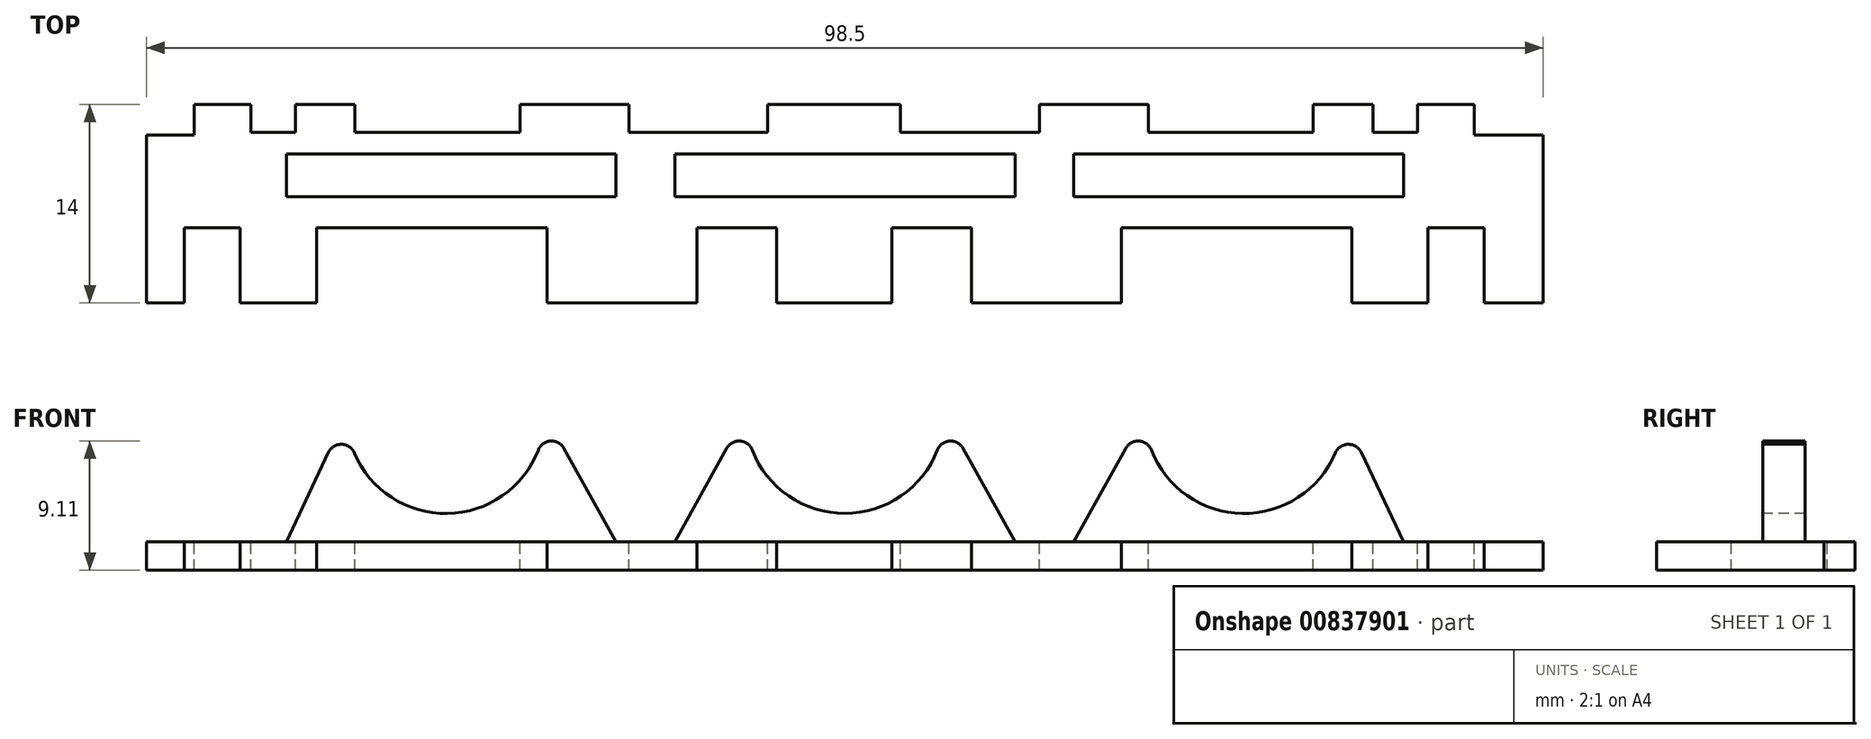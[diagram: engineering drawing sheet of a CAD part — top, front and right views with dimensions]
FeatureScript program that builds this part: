
annotation { "Feature Type Name" : "Feature", "Feature Type Description" : "" }
export const myFeature = defineFeature(function(context is Context, id is Id, definition is map)
    precondition{}
    {
        {
            var Q0;
            Q0=qCreatedBy(makeId("Front.planeOp"),FACE);
            var sketch = newSketch(context, id + "F0", { "sketchPlane" : qUnion([Q0])});
            skLineSegment(sketch, "E0", {"start": v(-48.5, 0) * mm, "end": v(50, 0) * mm});
            skLineSegment(sketch, "E1", {"start": v(-48.5, 0) * mm, "end": v(-48.5, 2) * mm});
            skLineSegment(sketch, "E2", {"start": v(50, 0) * mm, "end": v(50, 2) * mm});
            skLineSegment(sketch, "E3", {"start": v(-48.5, 2) * mm, "end": v(50, 2) * mm});
            skArc(sketch, "E4", {"start": v(-34.4, 11) * mm, "mid": v(-27.4, 4) * mm, "end": v(-20.4, 11) * mm});
            skLineSegment(sketch, "E5", {"start": v(-48.5, 2) * mm, "end": v(-48.5, 23.42) * mm, "construction": true});
            skLineSegment(sketch, "E6", {"start": v(-34.4, 11) * mm, "end": v(-38.65, 2) * mm});
            skLineSegment(sketch, "E7.MirrorCS", {"start": v(-20.4, 11) * mm, "end": v(-15.4, 2) * mm});
            skLineSegment(sketch, "E8", {"start": v(0.75, 2) * mm, "end": v(0.75, 4) * mm});
            skArc(sketch, "E9", {"start": v(-6.25, 11) * mm, "mid": v(-4.2, 6.05) * mm, "end": v(0.75, 4) * mm});
            skLineSegment(sketch, "E10", {"start": v(-6.25, 11) * mm, "end": v(-11.25, 2) * mm});
            skPoint(sketch, "E11.end.orphan", {"position": v(-26.65, 2) * mm});
            skArc(sketch, "E12.MirrorCS", {"start": v(7.75, 11) * mm, "mid": v(5.7, 6.05) * mm, "end": v(0.75, 4) * mm});
            skLineSegment(sketch, "E13.MirrorCS", {"start": v(7.75, 11) * mm, "end": v(12.75, 2) * mm});
            skLineSegment(sketch, "E14.MirrorCS", {"start": v(21.9, 11) * mm, "end": v(16.9, 2) * mm});
            skArc(sketch, "E15.MirrorCS", {"start": v(35.9, 11) * mm, "mid": v(28.9, 4) * mm, "end": v(21.9, 11) * mm});
            skLineSegment(sketch, "E16.MirrorCS", {"start": v(35.9, 11) * mm, "end": v(40.15, 2) * mm});
            skSolve(sketch);
        }
        {
            var Q0;
            Q0=makeQuery(id+"F0.imprint","IMPRINT",FACE,{"disambiguationData":[TD([[makeQuery(id+"F0.imprint","IMPRINT",EDGE,{"derivedFrom":sQuery(id+"F0.wireOp",EDGE,"E0")}),1.0]])]});
            extrude(context, id + "F1", {"entities" : qUnion([Q0]), "depth" : 7.5 * mm, "offsetDistance" : 25 * mm});
        }
        {
            var Q0;
            {var subQ0=sQuery(id+"F0.wireOp",EDGE,"E14.MirrorCS");Q0=makeQuery(id+"F0.imprint","IMPRINT",FACE,{"disambiguationData":[TD([[makeQuery(id+"F0.imprint","IMPRINT",EDGE,{"derivedFrom":subQ0}),1.0]])]});}
            var Q1;
            {var subQ0=sQuery(id+"F0.wireOp",EDGE,"E8");Q1=makeQuery(id+"F0.imprint","IMPRINT",FACE,{"disambiguationData":[TD([[makeQuery(id+"F0.imprint","IMPRINT",EDGE,{"derivedFrom":subQ0}),-1.0]])]});}
            var Q2;
            {var subQ0=sQuery(id+"F0.wireOp",EDGE,"E8");Q2=makeQuery(id+"F0.imprint","IMPRINT",FACE,{"disambiguationData":[TD([[makeQuery(id+"F0.imprint","IMPRINT",EDGE,{"derivedFrom":subQ0}),1.0]])]});}
            var Q3;
            Q3=makeQuery(id+"F0.imprint","IMPRINT",FACE,{"disambiguationData":[TD([[makeQuery(id+"F0.imprint","IMPRINT",EDGE,{"derivedFrom":sQuery(id+"F0.wireOp",EDGE,"E4")}),-1.0]])]});
            var Q4;
            Q4=makeQuery(id+"F0.imprint","IMPRINT",FACE,{"disambiguationData":[TD([[makeQuery(id+"F0.imprint","IMPRINT",EDGE,{"derivedFrom":sQuery(id+"F0.wireOp",EDGE,"E0")}),1.0]])]});
            extrude(context, id + "F2", {"entities" : qUnion([Q0, Q1, Q2, Q3, Q4]), "operationType" : NewBodyOperationType.ADD, "oppositeDirection" : true, "depth" : 3 * mm, "offsetDistance" : 25 * mm});
        }
        {
            var Q0;
            Q0=makeQuery(id+"F0.imprint","IMPRINT",FACE,{"disambiguationData":[TD([[makeQuery(id+"F0.imprint","IMPRINT",EDGE,{"derivedFrom":sQuery(id+"F0.wireOp",EDGE,"E0")}),1.0]])]});
            extrude(context, id + "F3", {"entities" : qUnion([Q0]), "operationType" : NewBodyOperationType.ADD, "oppositeDirection" : true, "depth" : 6.5 * mm, "offsetDistance" : 25 * mm});
        }
        {
            var Q0;
            {var subQ0=sQuery(id+"F0.wireOp",EDGE,"E3");Q0=makeQuery(id+"F3.boolean.opBoolean","MERGE",FACE,{"derivedFrom":[makeQuery(id+"F2.boolean.opBoolean","MERGE",FACE,{"derivedFrom":[makeQuery(id+"F1.opExtrude","SWEPT_FACE",FACE,{"disambiguationData":[OSD([subQ0])]}),makeQuery(id+"F2.opExtrude","SWEPT_FACE",FACE,{"disambiguationData":[OSD([subQ0]),TDD([makeQuery(id+"F0.imprint","IMPRINT",EDGE,{"disambiguationData":[TD([[makeQuery(id+"F0.imprint","INTERSECT",VERTEX,{"derivedFrom":[sQuery(id+"F0.wireOp",EDGE,"E1"),subQ0]}),-1.0]])],"derivedFrom":subQ0})])]}),makeQuery(id+"F2.opExtrude","SWEPT_FACE",FACE,{"disambiguationData":[OSD([subQ0]),TDD([makeQuery(id+"F0.imprint","IMPRINT",EDGE,{"disambiguationData":[TD([[makeQuery(id+"F0.imprint","INTERSECT",VERTEX,{"derivedFrom":[subQ0,sQuery(id+"F0.wireOp",EDGE,"E7.MirrorCS")]}),-1.0]])],"derivedFrom":subQ0})])]}),makeQuery(id+"F2.opExtrude","SWEPT_FACE",FACE,{"disambiguationData":[OSD([subQ0]),TDD([makeQuery(id+"F0.imprint","IMPRINT",EDGE,{"disambiguationData":[TD([[makeQuery(id+"F0.imprint","INTERSECT",VERTEX,{"derivedFrom":[subQ0,sQuery(id+"F0.wireOp",EDGE,"E13.MirrorCS")]}),-1.0]])],"derivedFrom":subQ0})])]}),makeQuery(id+"F2.opExtrude","SWEPT_FACE",FACE,{"disambiguationData":[OSD([subQ0]),TDD([makeQuery(id+"F0.imprint","IMPRINT",EDGE,{"disambiguationData":[TD([[makeQuery(id+"F0.imprint","INTERSECT",VERTEX,{"derivedFrom":[sQuery(id+"F0.wireOp",EDGE,"E2"),subQ0]}),1.0]])],"derivedFrom":subQ0})])]})]}),makeQuery(id+"F3.opExtrude","SWEPT_FACE",FACE,{"disambiguationData":[OSD([subQ0])]})]});}
            var sketch = newSketch(context, id + "F4", { "sketchPlane" : qUnion([Q0])});
            skLineSegment(sketch, "E17.bottom", {"start": v(45.83, -7.5) * mm, "end": v(41.9, -7.5) * mm});
            skLineSegment(sketch, "E17.top", {"start": v(45.83, -2.2) * mm, "end": v(41.9, -2.2) * mm});
            skLineSegment(sketch, "E17.left", {"start": v(45.83, -7.5) * mm, "end": v(45.83, -2.2) * mm});
            skLineSegment(sketch, "E17.right", {"start": v(41.9, -7.5) * mm, "end": v(41.9, -2.2) * mm});
            skLineSegment(sketch, "E18.bottom", {"start": v(36.53, -7.5) * mm, "end": v(20.26, -7.5) * mm});
            skLineSegment(sketch, "E18.top", {"start": v(36.53, -2.2) * mm, "end": v(20.26, -2.2) * mm});
            skLineSegment(sketch, "E18.left", {"start": v(36.53, -7.5) * mm, "end": v(36.53, -2.2) * mm});
            skLineSegment(sketch, "E18.right", {"start": v(20.26, -7.5) * mm, "end": v(20.26, -2.2) * mm});
            skLineSegment(sketch, "E19.bottom", {"start": v(9.7, -7.5) * mm, "end": v(4.07, -7.5) * mm});
            skLineSegment(sketch, "E19.top", {"start": v(9.7, -2.2) * mm, "end": v(4.07, -2.2) * mm});
            skLineSegment(sketch, "E19.left", {"start": v(9.7, -7.5) * mm, "end": v(9.7, -2.2) * mm});
            skLineSegment(sketch, "E19.right", {"start": v(4.07, -7.5) * mm, "end": v(4.07, -2.2) * mm});
            skLineSegment(sketch, "E20.bottom", {"start": v(50, 4.33) * mm, "end": v(45.15, 4.33) * mm});
            skLineSegment(sketch, "E20.top", {"start": v(50, 6.5) * mm, "end": v(45.15, 6.5) * mm});
            skLineSegment(sketch, "E20.left", {"start": v(50, 4.33) * mm, "end": v(50, 6.5) * mm});
            skLineSegment(sketch, "E20.right", {"start": v(45.15, 4.33) * mm, "end": v(45.15, 6.5) * mm});
            skLineSegment(sketch, "E21.bottom", {"start": v(33.8, 6.5) * mm, "end": v(22.16, 6.5) * mm});
            skLineSegment(sketch, "E21.top", {"start": v(33.8, 4.54) * mm, "end": v(22.16, 4.54) * mm});
            skLineSegment(sketch, "E21.left", {"start": v(33.8, 6.5) * mm, "end": v(33.8, 4.54) * mm});
            skLineSegment(sketch, "E21.right", {"start": v(22.16, 6.5) * mm, "end": v(22.16, 4.54) * mm});
            skLineSegment(sketch, "E22.bottom", {"start": v(41.15, 6.5) * mm, "end": v(38, 6.5) * mm});
            skLineSegment(sketch, "E22.top", {"start": v(41.15, 4.54) * mm, "end": v(38, 4.54) * mm});
            skLineSegment(sketch, "E22.left", {"start": v(41.15, 6.5) * mm, "end": v(41.15, 4.54) * mm});
            skLineSegment(sketch, "E22.right", {"start": v(38, 6.5) * mm, "end": v(38, 4.54) * mm});
            skLineSegment(sketch, "E23.bottom", {"start": v(14.47, 6.5) * mm, "end": v(4.68, 6.5) * mm});
            skLineSegment(sketch, "E23.top", {"start": v(14.47, 4.54) * mm, "end": v(4.68, 4.54) * mm});
            skLineSegment(sketch, "E23.left", {"start": v(14.47, 6.5) * mm, "end": v(14.47, 4.54) * mm});
            skLineSegment(sketch, "E23.right", {"start": v(4.68, 6.5) * mm, "end": v(4.68, 4.54) * mm});
            skLineSegment(sketch, "E24.MirrorCS", {"start": v(-4.07, -7.5) * mm, "end": v(-4.07, -2.2) * mm});
            skLineSegment(sketch, "E25.MirrorCS", {"start": v(-9.7, -2.2) * mm, "end": v(-4.07, -2.2) * mm});
            skLineSegment(sketch, "E26.MirrorCS", {"start": v(-9.7, -7.5) * mm, "end": v(-9.7, -2.2) * mm});
            skLineSegment(sketch, "E27.MirrorCS", {"start": v(-4.68, 6.5) * mm, "end": v(-4.68, 4.54) * mm});
            skLineSegment(sketch, "E28.MirrorCS", {"start": v(-14.47, 4.54) * mm, "end": v(-4.68, 4.54) * mm});
            skLineSegment(sketch, "E29.MirrorCS", {"start": v(-14.47, 6.5) * mm, "end": v(-14.47, 4.54) * mm});
            skLineSegment(sketch, "E30.MirrorCS", {"start": v(-20.26, -7.5) * mm, "end": v(-20.26, -2.2) * mm});
            skLineSegment(sketch, "E31.MirrorCS", {"start": v(-36.53, -2.2) * mm, "end": v(-20.26, -2.2) * mm});
            skLineSegment(sketch, "E32.MirrorCS", {"start": v(-36.53, -7.5) * mm, "end": v(-36.53, -2.2) * mm});
            skLineSegment(sketch, "E33.MirrorCS", {"start": v(-22.16, 6.5) * mm, "end": v(-22.16, 4.54) * mm});
            skLineSegment(sketch, "E34.MirrorCS", {"start": v(-33.8, 4.54) * mm, "end": v(-22.16, 4.54) * mm});
            skLineSegment(sketch, "E35.MirrorCS", {"start": v(-33.8, 6.5) * mm, "end": v(-33.8, 4.54) * mm});
            skLineSegment(sketch, "E36.MirrorCS", {"start": v(-38, 6.5) * mm, "end": v(-38, 4.54) * mm});
            skLineSegment(sketch, "E37.MirrorCS", {"start": v(-41.15, 4.54) * mm, "end": v(-38, 4.54) * mm});
            skLineSegment(sketch, "E38.MirrorCS", {"start": v(-41.15, 6.5) * mm, "end": v(-41.15, 4.54) * mm});
            skLineSegment(sketch, "E39.MirrorCS", {"start": v(-41.9, -7.5) * mm, "end": v(-41.9, -2.2) * mm});
            skLineSegment(sketch, "E40.MirrorCS", {"start": v(-45.83, -2.2) * mm, "end": v(-41.9, -2.2) * mm});
            skLineSegment(sketch, "E41.MirrorCS", {"start": v(-45.83, -7.5) * mm, "end": v(-45.83, -2.2) * mm});
            skLineSegment(sketch, "E42.MirrorCS", {"start": v(-45.15, 4.33) * mm, "end": v(-45.15, 6.5) * mm});
            skLineSegment(sketch, "E43.MirrorCS", {"start": v(-50, 4.33) * mm, "end": v(-45.15, 4.33) * mm});
            skSolve(sketch);
        }
        {
            var Q0;
            Q0=makeQuery(id+"F4.imprint","IMPRINT",FACE,{"disambiguationData":[TD([[makeQuery(id+"F4.imprint","IMPRINT",EDGE,{"derivedFrom":sQuery(id+"F4.wireOp",EDGE,"E19.bottom")}),1.0]])]});
            var Q1;
            Q1=makeQuery(id+"F4.imprint","IMPRINT",FACE,{"disambiguationData":[TD([[makeQuery(id+"F4.imprint","IMPRINT",EDGE,{"derivedFrom":sQuery(id+"F4.wireOp",EDGE,"E20.bottom")}),-1.0]])]});
            var Q2;
            Q2=makeQuery(id+"F4.imprint","IMPRINT",FACE,{"disambiguationData":[TD([[makeQuery(id+"F4.imprint","IMPRINT",EDGE,{"derivedFrom":sQuery(id+"F4.wireOp",EDGE,"E21.bottom")}),-1.0]])]});
            var Q3;
            Q3=makeQuery(id+"F4.imprint","IMPRINT",FACE,{"disambiguationData":[TD([[makeQuery(id+"F4.imprint","IMPRINT",EDGE,{"derivedFrom":sQuery(id+"F4.wireOp",EDGE,"E22.bottom")}),-1.0]])]});
            var Q4;
            Q4=makeQuery(id+"F4.imprint","IMPRINT",FACE,{"disambiguationData":[TD([[makeQuery(id+"F4.imprint","IMPRINT",EDGE,{"derivedFrom":sQuery(id+"F4.wireOp",EDGE,"E23.bottom")}),-1.0]])]});
            var Q5;
            Q5=makeQuery(id+"F4.imprint","IMPRINT",FACE,{"disambiguationData":[TD([[makeQuery(id+"F4.imprint","IMPRINT",EDGE,{"derivedFrom":sQuery(id+"F4.wireOp",EDGE,"E18.bottom")}),1.0]])]});
            var Q6;
            Q6=makeQuery(id+"F4.imprint","IMPRINT",FACE,{"disambiguationData":[TD([[makeQuery(id+"F4.imprint","IMPRINT",EDGE,{"derivedFrom":sQuery(id+"F4.wireOp",EDGE,"E17.bottom")}),1.0]])]});
            var Q7;
            {var subQ0=sQuery(id+"F4.wireOp",EDGE,"E24.MirrorCS");Q7=makeQuery(id+"F4.imprint","IMPRINT",FACE,{"disambiguationData":[TD([[makeQuery(id+"F4.imprint","IMPRINT",EDGE,{"derivedFrom":subQ0}),1.0]])]});}
            var Q8;
            {var subQ0=sQuery(id+"F4.wireOp",EDGE,"E27.MirrorCS");Q8=makeQuery(id+"F4.imprint","IMPRINT",FACE,{"disambiguationData":[TD([[makeQuery(id+"F4.imprint","IMPRINT",EDGE,{"derivedFrom":subQ0}),-1.0]])]});}
            var Q9;
            {var subQ0=sQuery(id+"F4.wireOp",EDGE,"E30.MirrorCS");Q9=makeQuery(id+"F4.imprint","IMPRINT",FACE,{"disambiguationData":[TD([[makeQuery(id+"F4.imprint","IMPRINT",EDGE,{"derivedFrom":subQ0}),1.0]])]});}
            var Q10;
            {var subQ0=sQuery(id+"F4.wireOp",EDGE,"E33.MirrorCS");Q10=makeQuery(id+"F4.imprint","IMPRINT",FACE,{"disambiguationData":[TD([[makeQuery(id+"F4.imprint","IMPRINT",EDGE,{"derivedFrom":subQ0}),-1.0]])]});}
            var Q11;
            {var subQ0=sQuery(id+"F4.wireOp",EDGE,"E36.MirrorCS");Q11=makeQuery(id+"F4.imprint","IMPRINT",FACE,{"disambiguationData":[TD([[makeQuery(id+"F4.imprint","IMPRINT",EDGE,{"derivedFrom":subQ0}),-1.0]])]});}
            var Q12;
            {var subQ0=sQuery(id+"F4.wireOp",EDGE,"E39.MirrorCS");Q12=makeQuery(id+"F4.imprint","IMPRINT",FACE,{"disambiguationData":[TD([[makeQuery(id+"F4.imprint","IMPRINT",EDGE,{"derivedFrom":subQ0}),1.0]])]});}
            var Q13;
            {var subQ0=sQuery(id+"F4.wireOp",EDGE,"E42.MirrorCS");Q13=makeQuery(id+"F4.imprint","IMPRINT",FACE,{"disambiguationData":[TD([[makeQuery(id+"F4.imprint","IMPRINT",EDGE,{"derivedFrom":subQ0}),1.0]])]});}
            extrude(context, id + "F5", {"entities" : qUnion([Q0, Q1, Q2, Q3, Q4, Q5, Q6, Q7, Q8, Q9, Q10, Q11, Q12, Q13]), "operationType" : NewBodyOperationType.REMOVE, "oppositeDirection" : true, "depth" : 2 * mm, "offsetDistance" : 25 * mm});
        }
        {
            var Q0;
            Q0=makeQuery(id+"F2.opExtrude","SWEPT_EDGE",EDGE,{"disambiguationData":[OSD([sQuery(id+"F0.wireOp",EDGE,"E15.MirrorCS"),sQuery(id+"F0.wireOp",EDGE,"E16.MirrorCS")])]});
            var Q1;
            Q1=makeQuery(id+"F2.opExtrude","SWEPT_EDGE",EDGE,{"disambiguationData":[OSD([sQuery(id+"F0.wireOp",EDGE,"E14.MirrorCS"),sQuery(id+"F0.wireOp",EDGE,"E15.MirrorCS")])]});
            var Q2;
            Q2=makeQuery(id+"F2.opExtrude","SWEPT_EDGE",EDGE,{"disambiguationData":[OSD([sQuery(id+"F0.wireOp",EDGE,"E12.MirrorCS"),sQuery(id+"F0.wireOp",EDGE,"E13.MirrorCS")])]});
            var Q3;
            Q3=makeQuery(id+"F2.opExtrude","SWEPT_EDGE",EDGE,{"disambiguationData":[OSD([sQuery(id+"F0.wireOp",EDGE,"E9"),sQuery(id+"F0.wireOp",EDGE,"E10")])]});
            var Q4;
            Q4=makeQuery(id+"F2.opExtrude","SWEPT_EDGE",EDGE,{"disambiguationData":[OSD([sQuery(id+"F0.wireOp",EDGE,"E4"),sQuery(id+"F0.wireOp",EDGE,"E7.MirrorCS")])]});
            var Q5;
            Q5=makeQuery(id+"F2.opExtrude","SWEPT_EDGE",EDGE,{"disambiguationData":[OSD([sQuery(id+"F0.wireOp",EDGE,"E4"),sQuery(id+"F0.wireOp",EDGE,"E6")])]});
            fillet(context, id + "F6", {"entities" : qUnion([Q0, Q1, Q2, Q3, Q4, Q5]), "radius" : 1 * mm, "tangentPropagation" : true, "allowEdgeOverflow" : false});
        }
    });
